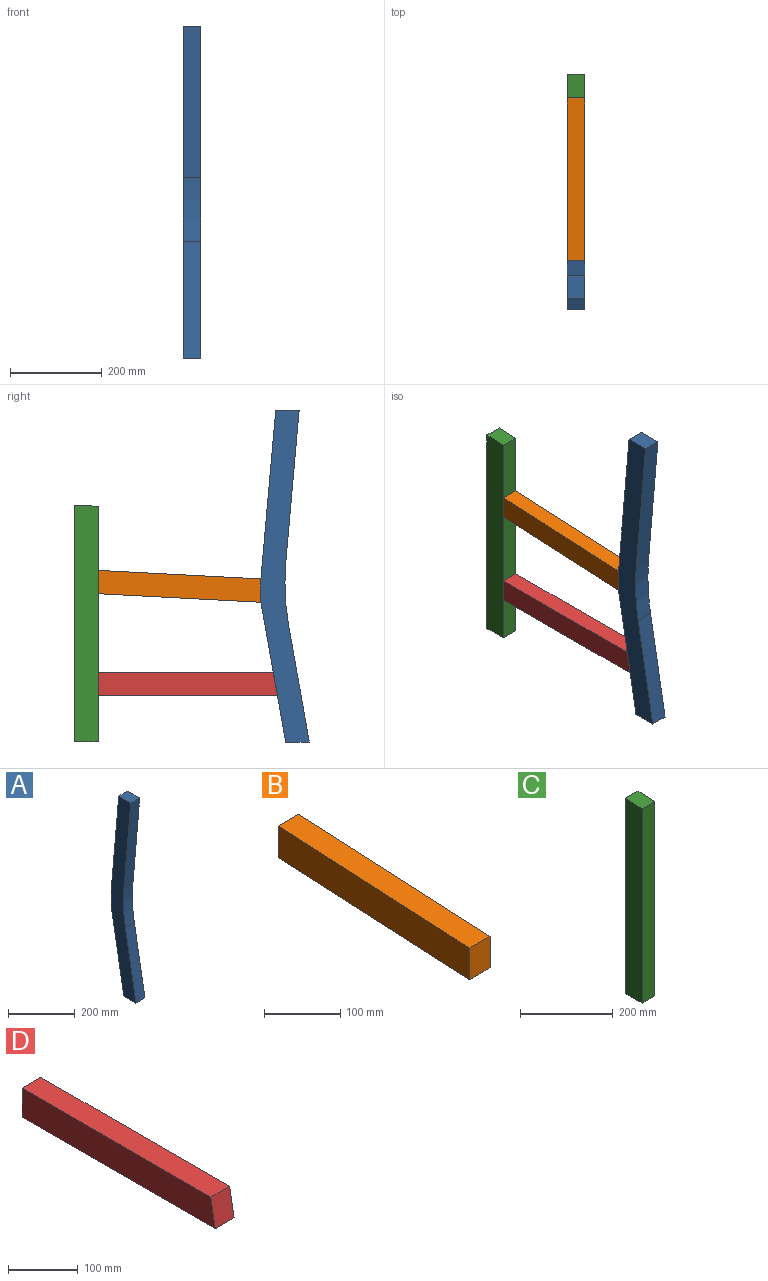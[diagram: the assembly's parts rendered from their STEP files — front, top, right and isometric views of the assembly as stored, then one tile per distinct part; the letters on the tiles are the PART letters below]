
ASSEMBLY  parts=4 mates=3
PART A: 10 faces, bbox 38.1x105.3x723.9 mm
  f0: plane 50.8x38.1mm, normal (0,1,0), area 1935.5mm2, adj f2,f3,f4,f8
  f1: plane 51.58x38.1mm, normal (0,0,-1), area 1965.3mm2, adj f2,f3,f4,f5
  f2: plane 723.9x105.33mm, normal (1,0,0), area 37243.6mm2, adj f0,f1,f4,f5,f6,f7,f8,f9
  f3: plane 723.9x105.33mm, normal (-1,0,0), area 37243.6mm2, adj f0,f1,f4,f5,f6,f7,f8,f9
  f4: plane 304.8x53.74mm, normal (0,0.98,-0.17), area 11792mm2, adj f0,f1,f2,f3
  f5: plane 254.73x44.92mm, normal (0,-0.98,0.17), area 9854.7mm2, adj f1,f2,f3,f9
  f6: plane 330.06x38.1mm, normal (0,-1,-0.09), area 12623.4mm2, adj f2,f3,f7,f9
  f7: plane 50.99x38.1mm, normal (0,0,1), area 1942.9mm2, adj f2,f3,f6,f8
  f8: plane 368.3x38.1mm, normal (0,1,0.09), area 14085.8mm2, adj f0,f2,f3,f7
  f9: cylinder r=533.4mm len=139.11mm, axis (-1,0,0), area 5320.4mm2, adj f2,f3,f5,f6
PART B: 6 faces, bbox 38.1x355.1x69.5 mm
  f0: plane 50.87x38.1mm, normal (0,-1,0), area 1938.1mm2, adj f1,f3,f4,f5
  f1: plane 355.11x38.1mm, normal (0,0.05,-1), area 13548.4mm2, adj f0,f2,f4,f5
  f2: plane 50.87x38.1mm, normal (0,1,0), area 1938.1mm2, adj f1,f3,f4,f5
  f3: plane 355.11x38.1mm, normal (0,-0.05,1), area 13548.4mm2, adj f0,f2,f4,f5
  f4: plane 355.11x69.48mm, normal (1,0,0), area 18064.5mm2, adj f0,f1,f2,f3
  f5: plane 355.11x69.48mm, normal (-1,0,0), area 18064.5mm2, adj f0,f1,f2,f3
PART C: 6 faces, bbox 38.1x50.8x516.6 mm
  f0: plane 513.91x38.1mm, normal (0,-1,0), area 19579.9mm2, adj f1,f3,f4,f5
  f1: plane 50.8x38.1mm, normal (0,0,-1), area 1935.5mm2, adj f0,f2,f4,f5
  f2: plane 516.57x38.1mm, normal (0,1,0), area 19681.3mm2, adj f1,f3,f4,f5
  f3: plane 50.8x38.1mm, normal (0,-0.05,1), area 1938.1mm2, adj f0,f2,f4,f5
  f4: plane 516.57x50.8mm, normal (1,0,0), area 26174.1mm2, adj f0,f1,f2,f3
  f5: plane 516.57x50.8mm, normal (-1,0,0), area 26174.1mm2, adj f0,f1,f2,f3
PART D: 6 faces, bbox 38.1x390.9x50.8 mm
  f0: plane 381.98x38.1mm, normal (0,0,1), area 14553.6mm2, adj f1,f3,f4,f5
  f1: plane 50.8x38.1mm, normal (0,-0.98,0.17), area 1965.3mm2, adj f0,f2,f4,f5
  f2: plane 390.94x38.1mm, normal (0,0,-1), area 14894.9mm2, adj f1,f3,f4,f5
  f3: plane 50.8x38.1mm, normal (0,1,0), area 1935.5mm2, adj f0,f2,f4,f5
  f4: plane 390.94x50.8mm, normal (-1,0,0), area 19632.3mm2, adj f0,f1,f2,f3
  f5: plane 390.94x50.8mm, normal (1,0,0), area 19632.3mm2, adj f0,f1,f2,f3
PLACE A t=(-19.05,9.69,381)mm
PLACE B t=(-76.2,-10.93,-25.54)mm
PLACE C t=(-76.2,-11.34,-25.47)mm
PLACE D t=(0,1.84,-25.4)mm
MATE fastened A.f0 <-> B.f0  axis (0,1,0) through (-19.05,79.54,355.6)mm
MATE fastened C.f0 <-> D.f3  axis (0,-1,0) through (0,434.65,0)mm
MATE fastened B.f2 <-> C.f0  axis (0,1,0) through (0,434.65,374.21)mm
